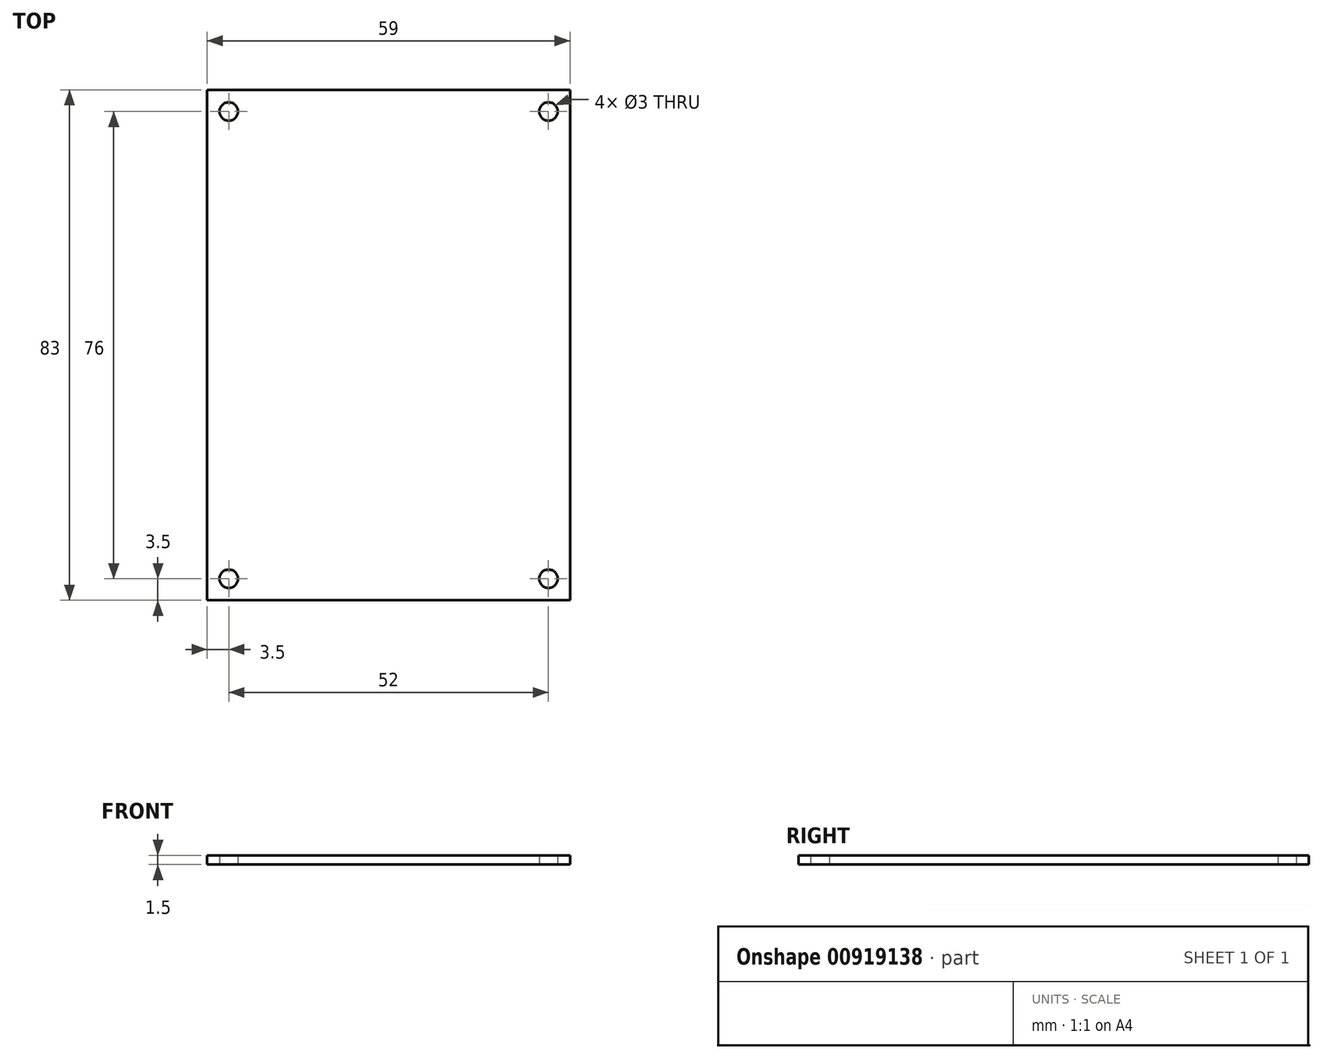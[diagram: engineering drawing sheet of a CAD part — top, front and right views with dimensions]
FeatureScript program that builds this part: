
annotation { "Feature Type Name" : "Feature", "Feature Type Description" : "" }
export const myFeature = defineFeature(function(context is Context, id is Id, definition is map)
    precondition{}
    {
        {
            var Q0;
            Q0=qCreatedBy(makeId("Top.planeOp"),FACE);
            var sketch = newSketch(context, id + "F0", { "sketchPlane" : qUnion([Q0])});
            skLineSegment(sketch, "E0.bottom", {"start": v(29.5, -41.5) * mm, "end": v(-29.5, -41.5) * mm});
            skLineSegment(sketch, "E0.top", {"start": v(29.5, 41.5) * mm, "end": v(-29.5, 41.5) * mm});
            skLineSegment(sketch, "E0.left", {"start": v(29.5, -41.5) * mm, "end": v(29.5, 41.5) * mm});
            skLineSegment(sketch, "E0.right", {"start": v(-29.5, -41.5) * mm, "end": v(-29.5, 41.5) * mm});
            skPoint(sketch, "E1.middle", {"position": v(0, 0) * mm});
            skCircle(sketch, "E2", {"center": v(26, 38) * mm, "radius": 1.5 * mm});
            skCircle(sketch, "E3", {"center": v(26, -38) * mm, "radius": 1.5 * mm});
            skCircle(sketch, "E4", {"center": v(-26, -38) * mm, "radius": 1.5 * mm});
            skCircle(sketch, "E5", {"center": v(-26, 38) * mm, "radius": 1.5 * mm});
            skLineSegment(sketch, "E6.bottom", {"start": v(26, -38) * mm, "end": v(-26, -38) * mm, "construction": true});
            skLineSegment(sketch, "E6.top", {"start": v(26, 38) * mm, "end": v(-26, 38) * mm, "construction": true});
            skLineSegment(sketch, "E6.left", {"start": v(26, -38) * mm, "end": v(26, 38) * mm, "construction": true});
            skLineSegment(sketch, "E6.right", {"start": v(-26, -38) * mm, "end": v(-26, 38) * mm, "construction": true});
            skLineSegment(sketch, "E7", {"start": v(-26, 38) * mm, "end": v(-26, 41.5) * mm, "construction": true});
            skLineSegment(sketch, "E8", {"start": v(-26, 38) * mm, "end": v(-29.5, 38) * mm, "construction": true});
            skSolve(sketch);
        }
        {
            var Q0;
            Q0=qSketchRegion(id+"F0",true);
            extrude(context, id + "F1", {"entities" : qUnion([Q0]), "depth" : 1.5 * mm, "offsetDistance" : 25 * mm});
        }
    });
